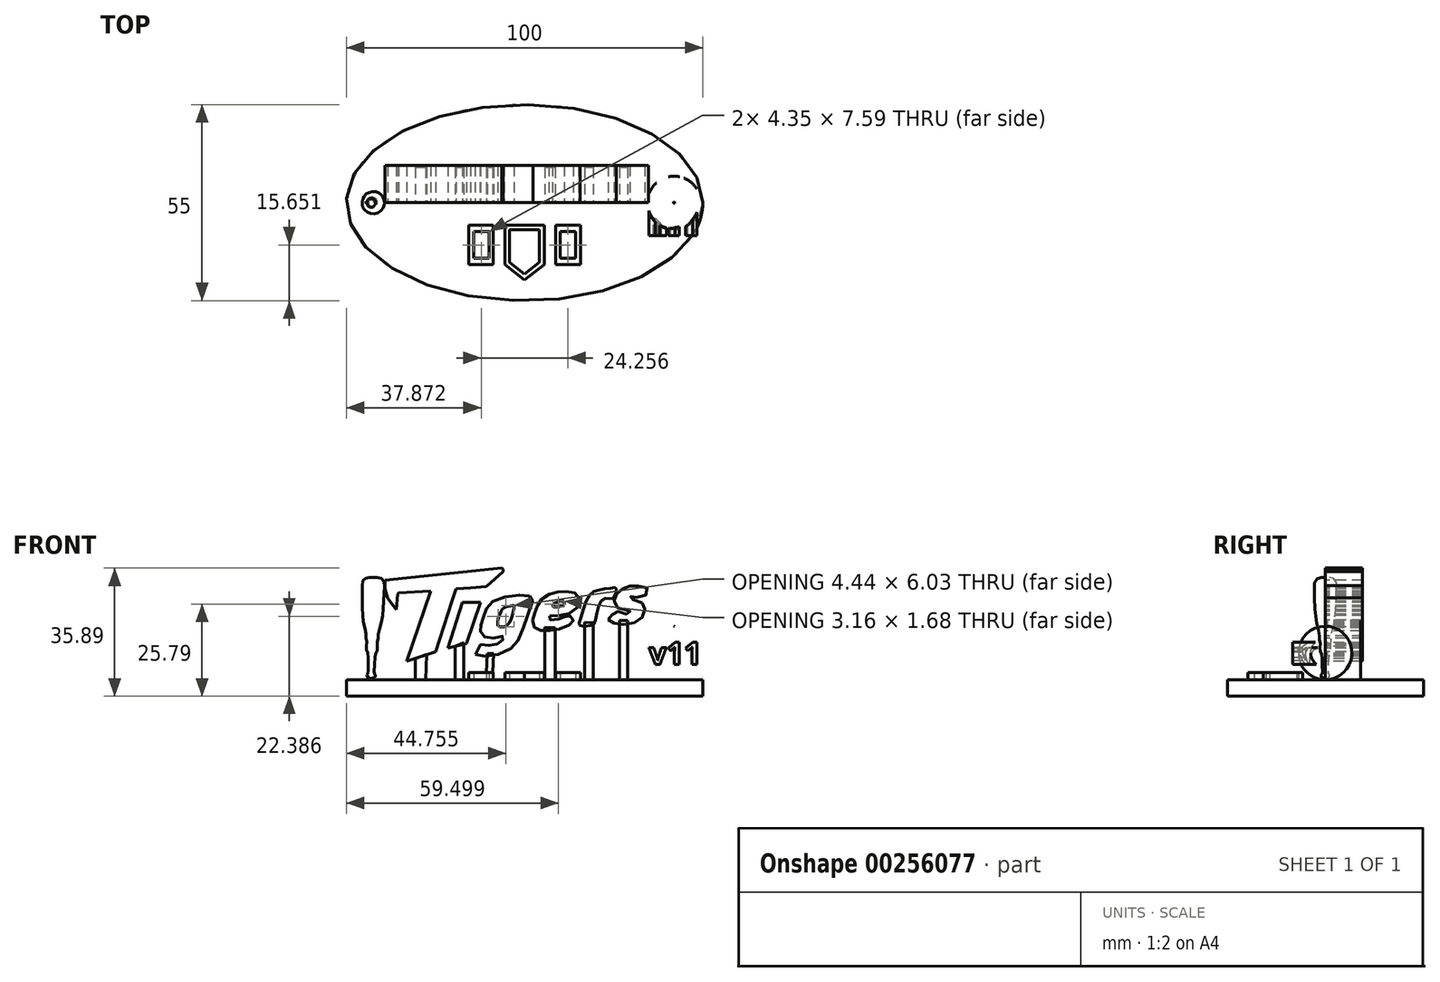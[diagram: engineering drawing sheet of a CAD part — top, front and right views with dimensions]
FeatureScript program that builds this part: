
annotation { "Feature Type Name" : "Feature", "Feature Type Description" : "" }
export const myFeature = defineFeature(function(context is Context, id is Id, definition is map)
    precondition{}
    {
        {
            var Q0;
            Q0=qCreatedBy(makeId("Top.planeOp"),FACE);
            var sketch = newSketch(context, id + "F0", { "sketchPlane" : qUnion([Q0])});
            skEllipse(sketch, "E0", {"center": v(0, 0) * mm, "majorRadius": 50 * mm, "minorRadius": 27.5 * mm, "majorAxis": v(1, 0)});
            skSolve(sketch);
        }
        {
            var Q0;
            Q0=qCreatedBy(makeId("Front.planeOp"),FACE);
            var sketch = newSketch(context, id + "F1", { "sketchPlane" : qUnion([Q0])});
            skLineSegment(sketch, "E1", {"start": v(-36, 19.68) * mm, "end": v(-38.37, 22.87) * mm});
            skLineSegment(sketch, "E2", {"start": v(-38.37, 22.87) * mm, "end": v(-39.1, 25.54) * mm});
            skLineSegment(sketch, "E3", {"start": v(-39.1, 25.54) * mm, "end": v(-39.1, 27.18) * mm});
            skLineSegment(sketch, "E4", {"start": v(-39.1, 27.18) * mm, "end": v(-39.1, 27.88) * mm});
            skLineSegment(sketch, "E5", {"start": v(-39.1, 27.88) * mm, "end": v(-6.45, 31.3) * mm});
            skLineSegment(sketch, "E6", {"start": v(-6.45, 31.3) * mm, "end": v(-5.98, 30.96) * mm});
            skLineSegment(sketch, "E7", {"start": v(-5.98, 30.96) * mm, "end": v(-5.98, 30.25) * mm});
            skLineSegment(sketch, "E8", {"start": v(-5.98, 30.25) * mm, "end": v(-10.66, 26.15) * mm});
            skLineSegment(sketch, "E9", {"start": v(-10.66, 26.15) * mm, "end": v(-15.12, 25.7) * mm});
            skLineSegment(sketch, "E10", {"start": v(-15.12, 25.7) * mm, "end": v(-19.24, 25.53) * mm});
            skLineSegment(sketch, "E11", {"start": v(-19.24, 25.53) * mm, "end": v(-20.39, 22.02) * mm});
            skLineSegment(sketch, "E12", {"start": v(-20.39, 22.02) * mm, "end": v(-24.95, 7.86) * mm});
            skLineSegment(sketch, "E13", {"start": v(-24.95, 7.86) * mm, "end": v(-33.09, 5.19) * mm});
            skLineSegment(sketch, "E14", {"start": v(-33.09, 5.19) * mm, "end": v(-26.32, 24.86) * mm});
            skLineSegment(sketch, "E15", {"start": v(-26.32, 24.86) * mm, "end": v(-35.4, 24.37) * mm});
            skLineSegment(sketch, "E16", {"start": v(-35.4, 24.37) * mm, "end": v(-35.64, 24.03) * mm});
            skLineSegment(sketch, "E17", {"start": v(-35.64, 24.03) * mm, "end": v(-36, 19.68) * mm});
            skLineSegment(sketch, "E18", {"start": v(-21.52, 8.8) * mm, "end": v(-16.28, 10.16) * mm});
            skLineSegment(sketch, "E19", {"start": v(-16.28, 10.16) * mm, "end": v(-12.35, 21.7) * mm});
            skLineSegment(sketch, "E20", {"start": v(-12.35, 21.7) * mm, "end": v(-17.38, 21.7) * mm});
            skLineSegment(sketch, "E21", {"start": v(-17.38, 21.7) * mm, "end": v(-21.52, 8.8) * mm});
            skFitSpline(sketch, "E22", {"points": [v(-13.82, 7.02) * mm, v(-11.97, 6.6) * mm, v(-7.93, 6.9) * mm, v(-3.7, 8.86) * mm, v(-1.86, 10.98) * mm, v(-0.2, 15.13) * mm, v(0.8, 17.97) * mm, v(2.36, 23.06) * mm, v(1.66, 23.35) * mm, v(0.2, 23.64) * mm, v(-4.04, 23.54) * mm, v(-8.38, 22.2) * mm, v(-10.21, 20.66) * mm, v(-11.16, 18.7) * mm, v(-11.77, 16.9) * mm, v(-12.11, 15.7) * mm, v(-12.43, 14.42) * mm, v(-12.38, 13.5) * mm, v(-11.85, 12.38) * mm, v(-10.83, 11.91) * mm, v(-8.83, 11.7) * mm, v(-6.72, 11.98) * mm, v(-5.74, 12.3) * mm, v(-5.96, 11.34) * mm, v(-6.72, 10.5) * mm, v(-7.75, 9.98) * mm, v(-8.9, 9.63) * mm, v(-11.82, 9.7) * mm, v(-12.4, 9.8) * mm, v(-13.82, 7.02) * mm]});
            skFitSpline(sketch, "E23", {"points": [v(7.05, 17.92) * mm, v(10.2, 17.99) * mm, v(13.25, 18.94) * mm, v(15.53, 21.51) * mm, v(14.8, 23.84) * mm, v(12.32, 24.7) * mm, v(9.92, 24.7) * mm, v(7.45, 24.15) * mm, v(4.92, 22.7) * mm, v(3.67, 20.9) * mm, v(2.97, 19.03) * mm, v(2.32, 16.9) * mm, v(2.47, 15.13) * mm, v(3.59, 14.1) * mm, v(6.2, 13.73) * mm, v(9.12, 14.08) * mm, v(12.6, 15.33) * mm, v(13.72, 16.44) * mm, v(13.37, 17.29) * mm, v(12.45, 18.02) * mm, v(11.13, 17.58) * mm, v(10.17, 17.1) * mm, v(7.58, 16.79) * mm, v(6.9, 16.94) * mm, v(7.05, 17.92) * mm]});
            skFitSpline(sketch, "E24", {"points": [v(7.92, 20.57) * mm, v(10.04, 20.5) * mm, v(10.98, 21.17) * mm, v(11.08, 21.83) * mm, v(9.71, 21.98) * mm, v(8.52, 21.44) * mm, v(7.92, 20.57) * mm]});
            skFitSpline(sketch, "E25", {"points": [v(-4.68, 20.56) * mm, v(-6.25, 19.73) * mm, v(-7.58, 15.54) * mm, v(-6.96, 14.86) * mm, v(-4.68, 15.45) * mm, v(-2.92, 20.55) * mm, v(-3, 20.8) * mm, v(-4.68, 20.56) * mm]});
            skFitSpline(sketch, "E26", {"points": [v(15.44, 15.16) * mm, v(19, 15.36) * mm, v(19.8, 16.44) * mm, v(21.41, 21.93) * mm, v(23.35, 22.8) * mm, v(24.97, 22.99) * mm, v(25.66, 25.7) * mm, v(24.87, 25.76) * mm, v(21.06, 25.2) * mm, v(18, 23.36) * mm, v(15.47, 16.44) * mm, v(15.44, 15.16) * mm]});
            skFitSpline(sketch, "E27", {"points": [v(23.4, 16.91) * mm, v(24.91, 15.93) * mm, v(28.28, 15.5) * mm, v(32.4, 16.82) * mm, v(33.66, 19.42) * mm, v(33.4, 21.21) * mm, v(30.5, 22.4) * mm, v(29.57, 22.97) * mm, v(30.25, 23.54) * mm, v(32.36, 22.9) * mm, v(34.78, 25.12) * mm, v(32.76, 26.18) * mm, v(30, 26.31) * mm, v(27.84, 25.62) * mm, v(25.99, 24.2) * mm, v(25.12, 22.17) * mm, v(26, 20.3) * mm, v(28.09, 19.61) * mm, v(29.5, 19.38) * mm, v(29.52, 18.8) * mm, v(28.2, 18.36) * mm, v(25.79, 19.18) * mm, v(24.27, 18.02) * mm, v(23.4, 16.91) * mm]});
            skSolve(sketch);
        }
        {
            var Q0;
            Q0=makeQuery(id+"F0.imprint","IMPRINT",FACE,{"disambiguationData":[TD([[makeQuery(id+"F0.imprint","IMPRINT",EDGE,{"derivedFrom":sQuery(id+"F0.wireOp",EDGE,"E0")}),1.0]])]});
            extrude(context, id + "F2", {"entities" : qUnion([Q0]), "oppositeDirection" : true, "depth" : 4.6 * mm});
        }
        {
            var Q0;
            Q0 = qSketchRegion(id + "F1", true);
            extrude(context, id + "F3", {"entities" : qUnion([Q0]), "oppositeDirection" : true, "depth" : 10.4 * mm});
        }
        {
            var Q0;
            Q0=qCreatedBy(makeId("Front.planeOp"),FACE);
            var sketch = newSketch(context, id + "F4", { "sketchPlane" : qUnion([Q0])});
            skLineSegment(sketch, "E28", {"start": v(-30.66, 5.99) * mm, "end": v(-30.66, 0) * mm});
            skLineSegment(sketch, "E29", {"start": v(-30.66, 0) * mm, "end": v(-27.79, 0) * mm});
            skLineSegment(sketch, "E30", {"start": v(-27.79, 0) * mm, "end": v(-27.47, 7.05) * mm});
            skLineSegment(sketch, "E31", {"start": v(-19.41, 9.35) * mm, "end": v(-19.41, 0) * mm});
            skLineSegment(sketch, "E32", {"start": v(-19.41, 0) * mm, "end": v(-17, 0) * mm});
            skLineSegment(sketch, "E33", {"start": v(-17, 0) * mm, "end": v(-17, 10.4) * mm});
            skLineSegment(sketch, "E34", {"start": v(-10.49, 7.39) * mm, "end": v(-10.74, 0) * mm});
            skLineSegment(sketch, "E35", {"start": v(-10.74, 0) * mm, "end": v(-8.96, 0) * mm});
            skLineSegment(sketch, "E36", {"start": v(-8.96, 0) * mm, "end": v(-8.7, 7.33) * mm});
            skLineSegment(sketch, "E37", {"start": v(5.74, 14.67) * mm, "end": v(5.74, 0) * mm});
            skLineSegment(sketch, "E38", {"start": v(5.74, 0) * mm, "end": v(8.56, 0) * mm});
            skLineSegment(sketch, "E39", {"start": v(8.56, 0) * mm, "end": v(8.56, 14.57) * mm});
            skLineSegment(sketch, "E40", {"start": v(16.83, 16.05) * mm, "end": v(16.83, 0) * mm});
            skLineSegment(sketch, "E41", {"start": v(16.83, 0) * mm, "end": v(19.26, 0) * mm});
            skLineSegment(sketch, "E42", {"start": v(19.26, 0) * mm, "end": v(19.26, 16) * mm});
            skLineSegment(sketch, "E43", {"start": v(26.59, 16.55) * mm, "end": v(26.59, 0) * mm});
            skLineSegment(sketch, "E44", {"start": v(26.59, 0) * mm, "end": v(28.92, 0) * mm});
            skLineSegment(sketch, "E45", {"start": v(28.92, 0) * mm, "end": v(28.92, 16.6) * mm});
            skLineSegment(sketch, "E46", {"start": v(-30.66, 5.99) * mm, "end": v(-27.47, 7.05) * mm});
            skLineSegment(sketch, "E47", {"start": v(-19.41, 9.35) * mm, "end": v(-17, 10.4) * mm});
            skLineSegment(sketch, "E48", {"start": v(-10.49, 7.39) * mm, "end": v(-8.7, 7.33) * mm});
            skLineSegment(sketch, "E49", {"start": v(5.74, 14.67) * mm, "end": v(8.56, 14.57) * mm});
            skLineSegment(sketch, "E50", {"start": v(16.83, 16.05) * mm, "end": v(19.26, 16) * mm});
            skLineSegment(sketch, "E51", {"start": v(26.59, 16.55) * mm, "end": v(28.92, 16.6) * mm});
            skSolve(sketch);
        }
        {
            var Q0;
            Q0=makeQuery(id+"F4.imprint","IMPRINT",FACE,{"disambiguationData":[TD([[makeQuery(id+"F4.imprint","IMPRINT",EDGE,{"derivedFrom":sQuery(id+"F4.wireOp",EDGE,"E28")}),1.0]])]});
            var Q1;
            Q1=makeQuery(id+"F4.imprint","IMPRINT",FACE,{"disambiguationData":[TD([[makeQuery(id+"F4.imprint","IMPRINT",EDGE,{"derivedFrom":sQuery(id+"F4.wireOp",EDGE,"E31")}),1.0]])]});
            var Q2;
            Q2=makeQuery(id+"F4.imprint","IMPRINT",FACE,{"disambiguationData":[TD([[makeQuery(id+"F4.imprint","IMPRINT",EDGE,{"derivedFrom":sQuery(id+"F4.wireOp",EDGE,"E34")}),1.0]])]});
            var Q3;
            Q3=makeQuery(id+"F4.imprint","IMPRINT",FACE,{"disambiguationData":[TD([[makeQuery(id+"F4.imprint","IMPRINT",EDGE,{"derivedFrom":sQuery(id+"F4.wireOp",EDGE,"E37")}),1.0]])]});
            var Q4;
            Q4=makeQuery(id+"F4.imprint","IMPRINT",FACE,{"disambiguationData":[TD([[makeQuery(id+"F4.imprint","IMPRINT",EDGE,{"derivedFrom":sQuery(id+"F4.wireOp",EDGE,"E40")}),1.0]])]});
            var Q5;
            Q5=makeQuery(id+"F4.imprint","IMPRINT",FACE,{"disambiguationData":[TD([[makeQuery(id+"F4.imprint","IMPRINT",EDGE,{"derivedFrom":sQuery(id+"F4.wireOp",EDGE,"E43")}),1.0]])]});
            extrude(context, id + "F5", {"entities" : qUnion([Q0, Q1, Q2, Q3, Q4, Q5]), "oppositeDirection" : true, "depth" : 9.9 * mm});
        }
        {
            var Q0;
            Q0=qCreatedBy(makeId("Top.planeOp"),FACE);
            var sketch = newSketch(context, id + "F6", { "sketchPlane" : qUnion([Q0])});
            skLineSegment(sketch, "E52", {"start": v(-5.5, -6.38) * mm, "end": v(5.5, -6.38) * mm});
            skLineSegment(sketch, "E53", {"start": v(5.5, -6.38) * mm, "end": v(5.5, -17.38) * mm});
            skLineSegment(sketch, "E54", {"start": v(5.5, -17.38) * mm, "end": v(0, -21.7) * mm});
            skLineSegment(sketch, "E55", {"start": v(0, -21.7) * mm, "end": v(-5.5, -17.38) * mm});
            skLineSegment(sketch, "E56", {"start": v(-5.5, -17.38) * mm, "end": v(-5.5, -6.38) * mm});
            skLineSegment(sketch, "E57", {"start": v(-4.19, -7.56) * mm, "end": v(-4.19, -16.71) * mm});
            skLineSegment(sketch, "E58", {"start": v(-4.19, -16.71) * mm, "end": v(0, -20.04) * mm});
            skLineSegment(sketch, "E59", {"start": v(0, -20.04) * mm, "end": v(4.19, -16.71) * mm});
            skLineSegment(sketch, "E60", {"start": v(4.19, -16.71) * mm, "end": v(4.19, -7.56) * mm});
            skLineSegment(sketch, "E61", {"start": v(4.19, -7.56) * mm, "end": v(-4.19, -7.56) * mm});
            skLineSegment(sketch, "E62.bottom", {"start": v(-15.68, -6.38) * mm, "end": v(-8.74, -6.38) * mm});
            skLineSegment(sketch, "E62.top", {"start": v(-15.68, -17.38) * mm, "end": v(-8.74, -17.38) * mm});
            skLineSegment(sketch, "E62.left", {"start": v(-15.68, -6.38) * mm, "end": v(-15.68, -17.38) * mm});
            skLineSegment(sketch, "E62.right", {"start": v(-8.74, -6.38) * mm, "end": v(-8.74, -17.38) * mm});
            skLineSegment(sketch, "E63.bottom", {"start": v(-14.3, -8.05) * mm, "end": v(-9.96, -8.05) * mm});
            skLineSegment(sketch, "E63.top", {"start": v(-14.3, -15.65) * mm, "end": v(-9.96, -15.65) * mm});
            skLineSegment(sketch, "E63.left", {"start": v(-14.3, -8.05) * mm, "end": v(-14.3, -15.65) * mm});
            skLineSegment(sketch, "E63.right", {"start": v(-9.96, -8.05) * mm, "end": v(-9.96, -15.65) * mm});
            skLineSegment(sketch, "E64.MirrorCS", {"start": v(-8.74, -6.38) * mm, "end": v(-8.74, 4.62) * mm});
            skLineSegment(sketch, "E65", {"start": v(0, 0) * mm, "end": v(0, -27.58) * mm, "construction": true});
            skLineSegment(sketch, "E66.MirrorCS", {"start": v(15.68, -6.38) * mm, "end": v(8.74, -6.38) * mm});
            skLineSegment(sketch, "E67.MirrorCS", {"start": v(8.74, -6.38) * mm, "end": v(8.74, -17.38) * mm});
            skLineSegment(sketch, "E68.MirrorCS", {"start": v(15.68, -17.38) * mm, "end": v(8.74, -17.38) * mm});
            skLineSegment(sketch, "E69.MirrorCS", {"start": v(15.68, -6.38) * mm, "end": v(15.68, -17.38) * mm});
            skLineSegment(sketch, "E70.MirrorCS", {"start": v(14.3, -8.05) * mm, "end": v(9.96, -8.05) * mm});
            skLineSegment(sketch, "E71.MirrorCS", {"start": v(9.96, -8.05) * mm, "end": v(9.96, -15.65) * mm});
            skLineSegment(sketch, "E72.MirrorCS", {"start": v(14.3, -15.65) * mm, "end": v(9.96, -15.65) * mm});
            skLineSegment(sketch, "E73.MirrorCS", {"start": v(14.3, -8.05) * mm, "end": v(14.3, -15.65) * mm});
            skSolve(sketch);
        }
        {
            var Q0;
            Q0=makeQuery(id+"F6.imprint","IMPRINT",FACE,{"disambiguationData":[TD([[makeQuery(id+"F6.imprint","IMPRINT",EDGE,{"derivedFrom":sQuery(id+"F6.wireOp",EDGE,"E52")}),-1.0]])]});
            extrude(context, id + "F7", {"entities" : qUnion([Q0]), "operationType" : NewBodyOperationType.ADD, "depth" : 2 * mm});
        }
        {
            var Q0;
            Q0=makeQuery(id+"F6.imprint","IMPRINT",FACE,{"disambiguationData":[TD([[makeQuery(id+"F6.imprint","IMPRINT",EDGE,{"derivedFrom":sQuery(id+"F6.wireOp",EDGE,"E62.bottom")}),-1.0]])]});
            var Q1;
            Q1=makeQuery(id+"F6.imprint","IMPRINT",FACE,{"disambiguationData":[TD([[makeQuery(id+"F6.imprint","IMPRINT",EDGE,{"derivedFrom":sQuery(id+"F6.wireOp",EDGE,"E66.MirrorCS")}),1.0]])]});
            extrude(context, id + "F8", {"entities" : qUnion([Q0, Q1]), "depth" : 2 * mm});
        }
        {
            var Q0;
            Q0=qCreatedBy(makeId("Front.planeOp"),FACE);
            var sketch = newSketch(context, id + "F9", { "sketchPlane" : qUnion([Q0])});
            skLineSegment(sketch, "E74", {"start": v(41.94, 0) * mm, "end": v(41.94, 15) * mm});
            skArc(sketch, "E75", {"start": v(41.94, 0) * mm, "mid": v(49.52, 7.5) * mm, "end": v(41.94, 15) * mm});
            skSolve(sketch);
        }
        {
            var Q0;
            Q0 = qSketchRegion(id + "F9", true);
            var Q1;
            Q1=sQuery(id+"F9.wireOp",EDGE,"E74");
            revolve(context, id + "F10", {"operationType" : NewBodyOperationType.ADD, "entities" : qUnion([Q0]), "axis" : qUnion([Q1]), "revolveType" : RevolveType.FULL});
        }
        {
            var Q0;
            Q0=qCreatedBy(makeId("Front.planeOp"),FACE);
            var sketch = newSketch(context, id + "F11", { "sketchPlane" : qUnion([Q0])});
            skText(sketch, "E76", { "text": "v11", "fontName": "OpenSans-Bold.ttf"});
            const initialGuessF11  = {"E76": [0.03486, 0.00431, 1, 0, 0.00623]};
            skSetInitialGuess(sketch, initialGuessF11);
            skSolve(sketch);
        }
        {
            var Q0;
            Q0 = qSketchRegion(id + "F11", true);
            extrude(context, id + "F12", {"entities" : qUnion([Q0]), "operationType" : NewBodyOperationType.ADD, "depth" : 9.2 * mm});
        }
        {
            var Q0;
            Q0=qCreatedBy(makeId("Front.planeOp"),FACE);
            var sketch = newSketch(context, id + "F13", { "sketchPlane" : qUnion([Q0])});
            skLineSegment(sketch, "E77", {"start": v(-43.04, 0) * mm, "end": v(-42.35, 30.07) * mm});
            skFitSpline(sketch, "E78", {"points": [v(-42.38, 28.7) * mm, v(-41.32, 28.64) * mm, v(-39.7, 28.01) * mm, v(-39.33, 25.96) * mm, v(-39.6, 21.02) * mm, v(-40.06, 16.5) * mm, v(-40.98, 12.86) * mm, v(-41.1, 11.37) * mm, v(-41.36, 10.25) * mm, v(-41.32, 8.54) * mm, v(-41.65, 7.59) * mm, v(-41.82, 7.09) * mm, v(-42.2, 2.3) * mm, v(-42.21, 1.7) * mm, v(-41.9, 1.5) * mm, v(-41.8, 0.98) * mm, v(-41.99, 0.6) * mm, v(-43.04, 0.34) * mm], "startDerivative": vector(19.93, -0.21) * mm, "endDerivative": vector(-26.08, -3.76) * mm});
            skSolve(sketch);
        }
        {
            var Q0;
            {var subQ0=sQuery(id+"F13.wireOp",EDGE,"E78");Q0=makeQuery(id+"F13.imprint","IMPRINT",FACE,{"disambiguationData":[TD([[makeQuery(id+"F13.imprint","IMPRINT",EDGE,{"derivedFrom":subQ0}),-1.0]])]});}
            var Q1;
            Q1=sQuery(id+"F13.wireOp",EDGE,"E77");
            revolve(context, id + "F14", {"entities" : qUnion([Q0]), "axis" : qUnion([Q1]), "revolveType" : RevolveType.FULL});
        }
    });
